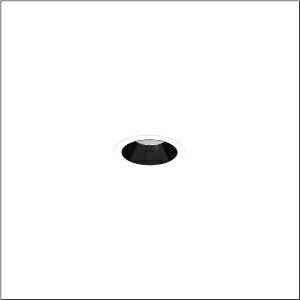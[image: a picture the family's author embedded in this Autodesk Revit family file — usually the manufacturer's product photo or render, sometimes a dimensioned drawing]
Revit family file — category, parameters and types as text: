
# Revit family: lunis_21_s_51db17ma91c
name_source: partatom
category: Lighting Fixtures
units: mm (PartAtom-declared; Revit-internal decimal feet)

## family parameters
Cut with Voids When Loaded = No
Host = Face
Light Source = No
Part Type = Normal
Room Calculation Point = No
Round Connector Dimension = Use Diameter
Shared = No

## types (1)
- --- (1 x LED, 830 lm, 5.9 W, 6500K)
    Apparent Load = 6 VA
    CIE Flux Codes = 97 100 100 100 100
    Color Rendering = 80
    Color Temperature = 6500K
    Default Elevation = 1800 mm
    Description = Lunis 21,  S, downlight, light control with lens, of PMMA, anti glare with reflector, of PC, light emission: direct distribution, LED rated luminous flux: 840lm, light colour: 830/840/865, with terminal, 3-pole, mains connection: 220..240V, AC, 50..60Hz, housing, round, of diecast aluminium, traffic white (RAL 9016), diameter: 84mm, clamping range: 1..40mm, protection rating (complete): IP20, protection rating (on room side): IP54, insulation class (complete): insulation class II (safety insulation), certification: CE, impact resistance: IK03, packaging unit: 1 piece
    Height = 0 mm  [stored 0 ft]
    Lamp = 1 x LED
    Lamp Light Flux = 830 lm
    Lamp Power = 5.9 W
    Lamp count = 1
    Length = 84 mm
    Luminous efficacy = 141 lm/W
    Manufacturer = Siteco
    ModVariant = No
    Model = 51DB17MA91C
    Mounting Place = Ceiling
    Mounting Type = Recessed
    Number of Poles = 1
    OnlyDefault = Yes
    Power Factor = 1
    Product Name = Lunis 21 S
    Product group = downlight
    ProductGroupID = 400
    Protection Class = Protection class II
    Protection Degree = IP 20
    RLX_Detail_Level = 1
    RLX_Emergency_Light_Flux = 0 lm
    RLX_Emergency_Type = 0
    RLX_Emergency_Type_DB = No
    RlxData = <blob elided: 8705 chars, md5=df4a4964>
    Socket = socket
    Standby Power = 0 W
    System Light Flux = 830 lm
    System Power = 6 W
    Type Comments = individual setting: colour temperature 6500K
    Type Image = l_1290844.jpg
    URL = http://relux.com
    VarID = @adj_020234
    Voltage = 0 V
    Weight = 0.00 kg
    Width = 0 mm  [stored 0 ft]

note: [stored X ft] marks values corroborated as IEEE doubles in the binary element streams (Revit-internal decimal feet)

## geometry (parser evidence)
native form markers: Sweep x8
no freeform markers — native parametric forms only
